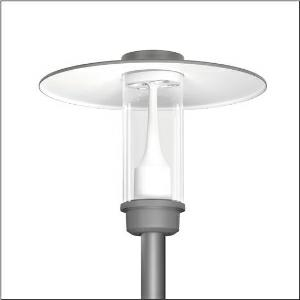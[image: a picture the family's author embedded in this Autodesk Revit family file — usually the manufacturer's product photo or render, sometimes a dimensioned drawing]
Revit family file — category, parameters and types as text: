
# Revit family: litepole_2_iq___p1_0a_5xa5425nf14h_2791
name_source: partatom
category: Lighting Fixtures
units: mm (PartAtom-declared; Revit-internal decimal feet)

## family parameters
Cut with Voids When Loaded = No
Host = Face
Light Source = No
Part Type = Normal
Room Calculation Point = No
Round Connector Dimension = Use Diameter
Shared = No

## types (1)
- --- (1 x LED, 1520 lm, 11.8 W, 2700K)
    Apparent Load = 12 VA
    CIE Flux Codes = 33 62 89 96 100
    Color Rendering = 70
    Color Temperature = 2700K
    Default Elevation = 1800 mm
    Description = Litepole 2 iQ, mast luminaire, Module 540 iQ-SR, primary light control with 3 zone facetted reflector, of plastic, silver coated, highly specular, structured, primary optical cover: cover, of PMMA, transparent, light distribution: P1.0a, light emission: direct distribution, primary light characteristic: strongly asymmetric, installation type: post-top, LED, High Power LED, rated luminous flux: 1.520lm, luminous efficacy: 129lm/W, light colour: 727, colour temperature: 2700K, control gear: iQ Street-Remote, control: pre-setting: logarithmic dimming characteristic, Street-Remote, Auto-Match, Temp-Guard, Lumen-Switch, Night-Set, Smart-Wire, Light-Fading, Desk-Remote (wireless, voltage-free reading and setting of iQ features in the workshop via application-optimized NFC function/RFID function), optimised constant luminous flux control (CLO 2.0), with terminal, 6-pole, max. 2.5mm², mains connection: 230..240V, AC, 50/60Hz, start of lifetime: 12W, end of service life: 12W, reduction: 6W, luminaire housing, upper part, of aluminium, coated, Siteco® metallic grey (DB 702S), diameter: 750mm, height: 590mm, spigot size: d x l = 76 x 70mm (post-top) | with reducer (optional accessory) 60 x 70mm, mounting height: 3..5m, post-top mast mounting element, of diecast aluminium, coated, Siteco® metallic grey (DB 702S), Module 540 iQ-SR, traffic white (RAL 9016), equipment: standard, protection rating (complete): IP65, insulation class (complete): insulation class II (safety insulation), certification: CE, ENEC, VDE, packaging unit: 1 piece

Light Distribution: P1.0a
    Height = 590 mm
    Lamp = 1 x LED
    Lamp Light Flux = 1520 lm
    Lamp Power = 11.8 W
    Lamp count = 1
    Length = 750 mm
    Luminous efficacy = 129 lm/W
    Manufacturer = Siteco
    ModVariant = No
    Model = 5XA5425NF14H
    Number of Poles = 1
    OnlyDefault = Yes
    Power Factor = 1
    Product Name = Litepole 2 iQ | P1.0a
    Product group = mast luminaire | pylon top
    ProductGroupID = 6100
    Protection Class = Protection class II
    Protection Degree = IP 65
    RLX_Detail_Level = 1
    RLX_Emergency_Light_Flux = 0 lm
    RLX_Emergency_Type = 0
    RLX_Emergency_Type_DB = No
    RlxData = <blob elided: 55361 chars, md5=4eaa78de>
    Socket = socket
    Standby Power = 0 W
    System Light Flux = 1520 lm
    System Power = 12 W
    Type Comments = factory setting: luminous flux: 100 % | dim-lin: 254 | 472 mA
    Type Image = l_1006518.jpg
    URL = http://relux.com
    VarID = @adj_152440
    Voltage = 0 V
    Weight = 0.00 kg
    Width = 0 mm  [stored 0 ft]

note: [stored X ft] marks values corroborated as IEEE doubles in the binary element streams (Revit-internal decimal feet)

## geometry (parser evidence)
native form markers: Blend x4, Sweep x9
no freeform markers — native parametric forms only
